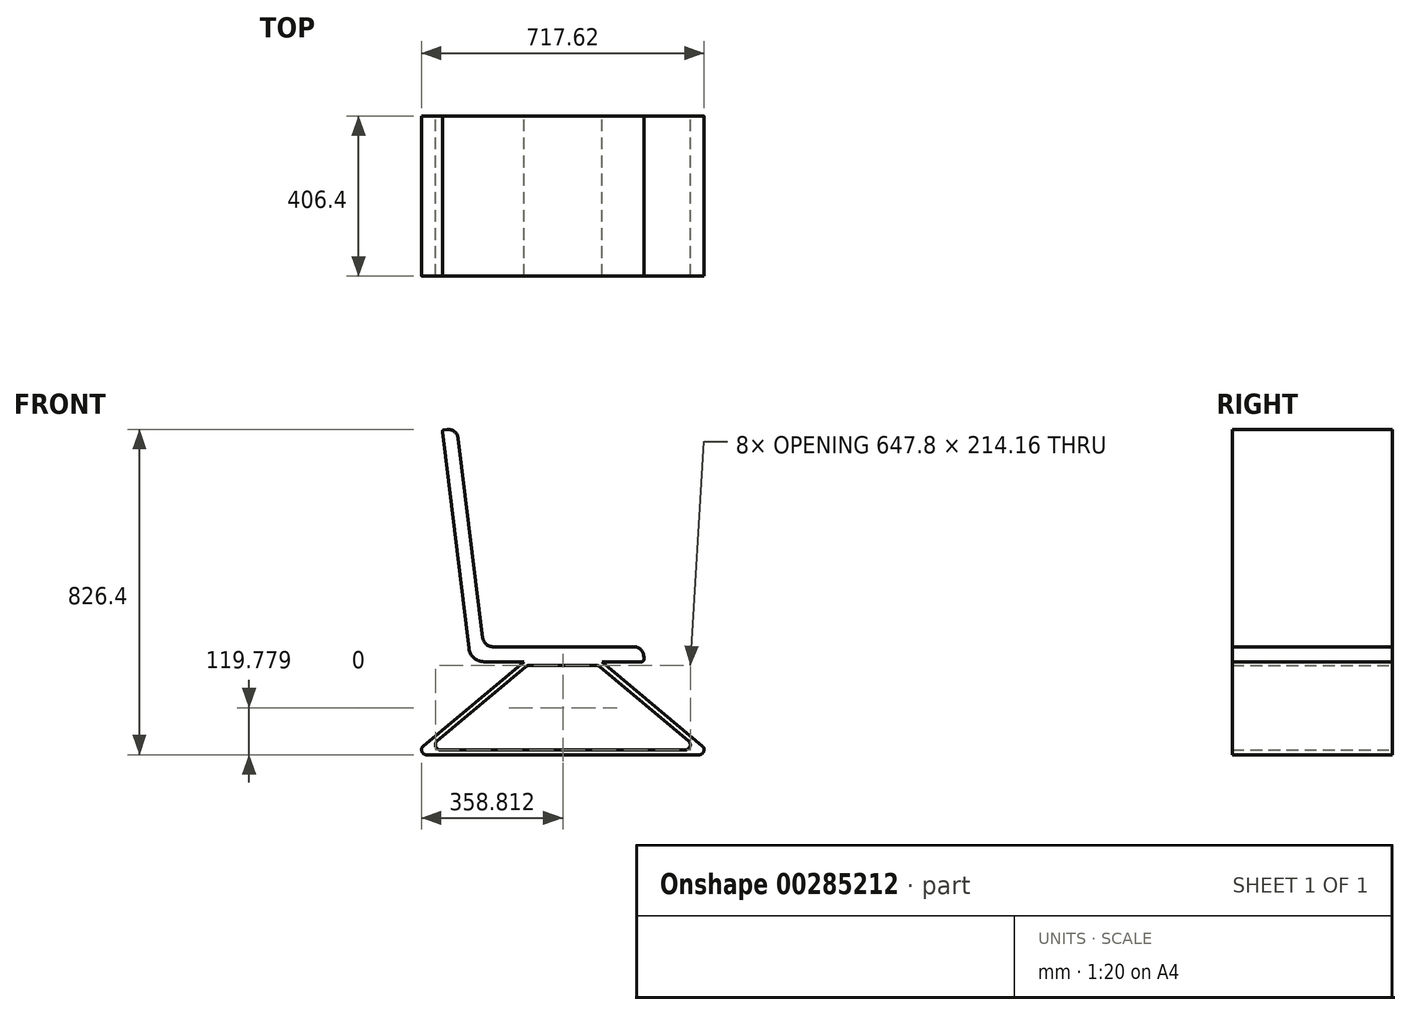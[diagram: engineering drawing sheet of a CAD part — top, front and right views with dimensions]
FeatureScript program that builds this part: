
annotation { "Feature Type Name" : "Feature", "Feature Type Description" : "" }
export const myFeature = defineFeature(function(context is Context, id is Id, definition is map)
    precondition{}
    {
        {
            var Q0;
            Q0=qCreatedBy(makeId("Front.planeOp"),FACE);
            var sketch = newSketch(context, id + "F0", { "sketchPlane" : qUnion([Q0])});
            skLineSegment(sketch, "E0", {"start": v(-256.16, 262.74) * mm, "end": v(-193.85, -244.37) * mm});
            skLineSegment(sketch, "E1", {"start": v(-168.64, -266.68) * mm, "end": v(189.9, -266.68) * mm});
            skLineSegment(sketch, "E2", {"start": v(-191.1, -266.68) * mm, "end": v(-191.1, -304.78) * mm});
            skLineSegment(sketch, "E3", {"start": v(215.3, -292.08) * mm, "end": v(215.3, -299.67) * mm});
            skLineSegment(sketch, "E4", {"start": v(-191.1, -304.78) * mm, "end": v(210.19, -304.78) * mm});
            skLineSegment(sketch, "E5", {"start": v(-284.47, 284.86) * mm, "end": v(-292.44, 283.88) * mm});
            skLineSegment(sketch, "E6", {"start": v(-191.1, -266.68) * mm, "end": v(-228.92, -271.32) * mm});
            skLineSegment(sketch, "E7", {"start": v(-296.5, 278.67) * mm, "end": v(-228.92, -271.32) * mm});
            skPoint(sketch, "E8.visualSharp", {"position": v(-191.1, -266.68) * mm});
            skArc(sketch, "E8.filletArc", {"start": v(-193.85, -244.37) * mm, "mid": v(-185.47, -260.3) * mm, "end": v(-168.64, -266.68) * mm});
            skArc(sketch, "E9", {"start": v(-228.92, -271.32) * mm, "mid": v(-216.35, -295.21) * mm, "end": v(-191.1, -304.78) * mm});
            skPoint(sketch, "E10.visualSharp", {"position": v(215.3, -266.68) * mm});
            skArc(sketch, "E10.filletArc", {"start": v(215.3, -292.08) * mm, "mid": v(207.85, -274.11) * mm, "end": v(189.9, -266.68) * mm});
            skPoint(sketch, "E11.visualSharp", {"position": v(215.3, -304.78) * mm});
            skArc(sketch, "E11.filletArc", {"start": v(210.19, -304.78) * mm, "mid": v(213.8, -303.28) * mm, "end": v(215.3, -299.67) * mm});
            skPoint(sketch, "E12.visualSharp", {"position": v(-259.26, 287.95) * mm});
            skArc(sketch, "E12.filletArc", {"start": v(-256.16, 262.74) * mm, "mid": v(-265.74, 279.66) * mm, "end": v(-284.47, 284.86) * mm});
            skPoint(sketch, "E13.visualSharp", {"position": v(-297.07, 283.3) * mm});
            skArc(sketch, "E13.filletArc", {"start": v(-292.44, 283.88) * mm, "mid": v(-295.55, 282.12) * mm, "end": v(-296.5, 278.67) * mm});
            skLineSegment(sketch, "E14", {"start": v(-89.5, -304.78) * mm, "end": v(-344.73, -518.93) * mm});
            skLineSegment(sketch, "E15", {"start": v(108.59, -304.78) * mm, "end": v(363.81, -518.93) * mm});
            skLineSegment(sketch, "E16", {"start": v(-336.57, -541.36) * mm, "end": v(355.65, -541.36) * mm});
            skPoint(sketch, "E17.visualSharp", {"position": v(-371.46, -541.36) * mm});
            skArc(sketch, "E17.filletArc", {"start": v(-344.73, -518.93) * mm, "mid": v(-348.5, -533) * mm, "end": v(-336.57, -541.36) * mm});
            skPoint(sketch, "E18.visualSharp", {"position": v(390.54, -541.36) * mm});
            skArc(sketch, "E18.filletArc", {"start": v(355.65, -541.36) * mm, "mid": v(367.58, -533) * mm, "end": v(363.81, -518.93) * mm});
            skLineSegment(sketch, "E19.0", {"start": v(-84.88, -317.47) * mm, "end": v(-309.84, -506.23) * mm});
            skLineSegment(sketch, "E20.0", {"start": v(-301.67, -528.66) * mm, "end": v(320.76, -528.66) * mm});
            skLineSegment(sketch, "E21.0", {"start": v(103.96, -317.47) * mm, "end": v(328.92, -506.23) * mm});
            skLineSegment(sketch, "E22", {"start": v(-76.72, -314.5) * mm, "end": v(95.8, -314.5) * mm});
            skArc(sketch, "E23.filletArc", {"start": v(320.76, -528.66) * mm, "mid": v(332.69, -520.3) * mm, "end": v(328.92, -506.23) * mm});
            skPoint(sketch, "E24.visualSharp", {"position": v(100.42, -314.5) * mm});
            skArc(sketch, "E24.filletArc", {"start": v(103.96, -317.47) * mm, "mid": v(100.14, -315.27) * mm, "end": v(95.8, -314.5) * mm});
            skPoint(sketch, "E25.visualSharp", {"position": v(-81.34, -314.5) * mm});
            skArc(sketch, "E25.filletArc", {"start": v(-76.72, -314.5) * mm, "mid": v(-81.06, -315.27) * mm, "end": v(-84.88, -317.47) * mm});
            skArc(sketch, "E26.filletArc", {"start": v(-309.84, -506.23) * mm, "mid": v(-313.6, -520.3) * mm, "end": v(-301.67, -528.66) * mm});
            skSolve(sketch);
        }
        {
            var Q0;
            Q0=makeQuery(id+"F0.imprint","IMPRINT",FACE,{"disambiguationData":[TD([[makeQuery(id+"F0.imprint","IMPRINT",EDGE,{"derivedFrom":sQuery(id+"F0.wireOp",EDGE,"E2")}),-1.0]])]});
            var Q1;
            Q1=makeQuery(id+"F0.imprint","IMPRINT",FACE,{"disambiguationData":[TD([[makeQuery(id+"F0.imprint","IMPRINT",EDGE,{"derivedFrom":sQuery(id+"F0.wireOp",EDGE,"E0")}),-1.0]])]});
            var Q2;
            {var subQ0=sQuery(id+"F0.wireOp",EDGE,"E14");Q2=makeQuery(id+"F0.imprint","IMPRINT",FACE,{"disambiguationData":[TD([[makeQuery(id+"F0.imprint","IMPRINT",EDGE,{"derivedFrom":subQ0}),1.0]])]});}
            extrude(context, id + "F1", {"entities" : qUnion([Q0, Q1, Q2]), "depth" : 406.4 * mm});
        }
    });
